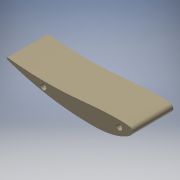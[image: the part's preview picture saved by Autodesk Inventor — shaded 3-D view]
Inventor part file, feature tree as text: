
AUTODESK INVENTOR PART (.ipt)
format: ipt  version: 2018 (Build 220112000, 112)  size: 125,440 bytes
history: native  units: mm
features: extrude x1, sketch x1, projected_geometry x1
ambient origin geometry x8: Origin, YZ Plane, XZ Plane, XY Plane, X Axis, Y Axis, Z Axis, Center Point
bodies: Body1 (feature_tree)
feature tree (3):
  extrude  "押し出し1"  Depth=40.2mm TaperAngle=0.0deg
  sketch  "スケッチ1"
  projected_geometry  "投影ループ1"
